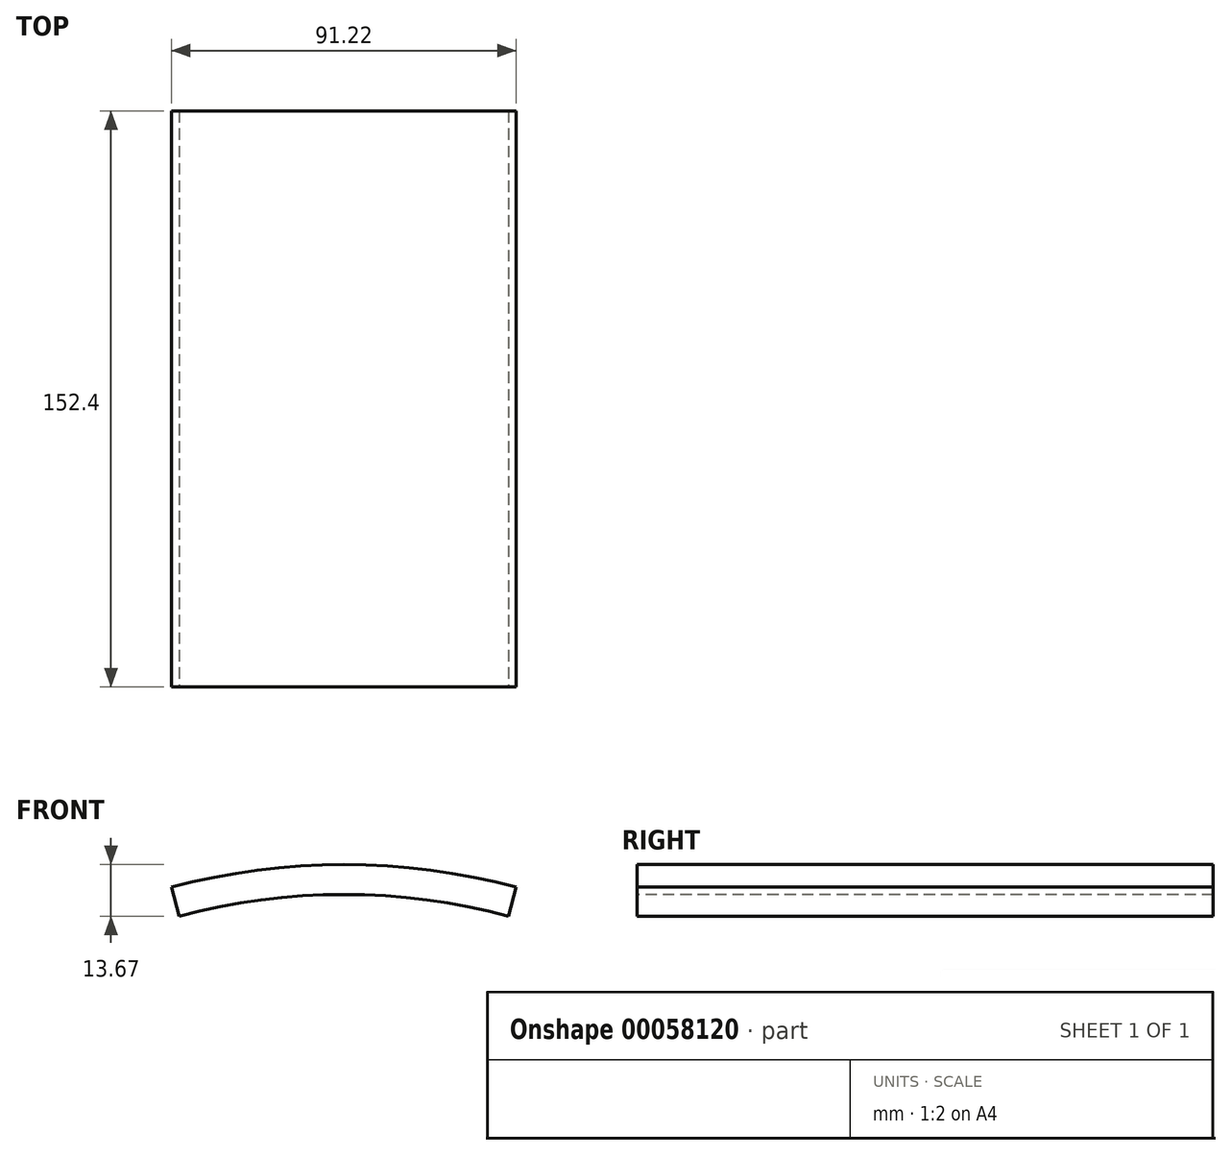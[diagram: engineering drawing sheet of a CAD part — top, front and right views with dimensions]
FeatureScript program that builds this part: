
annotation { "Feature Type Name" : "Feature", "Feature Type Description" : "" }
export const myFeature = defineFeature(function(context is Context, id is Id, definition is map)
    precondition{}
    {
        {
            var Q0;
            Q0=qCreatedBy(makeId("Front.planeOp"),FACE);
            var sketch = newSketch(context, id + "F0", { "sketchPlane" : qUnion([Q0])});
            skLineSegment(sketch, "E0.0", {"start": v(-47.64, 177.8) * mm, "end": v(47.64, 177.8) * mm});
            skPoint(sketch, "E0.0.midPoint", {"position": v(0, 177.8) * mm});
            skLineSegment(sketch, "E1.0", {"start": v(-40.84, 152.4) * mm, "end": v(40.84, 152.4) * mm});
            skPoint(sketch, "E1.0.midPoint", {"position": v(0, 152.4) * mm});
            skLineSegment(sketch, "E2", {"start": v(-47.64, 177.8) * mm, "end": v(-40.84, 152.4) * mm});
            skLineSegment(sketch, "E3", {"start": v(47.64, 177.8) * mm, "end": v(40.84, 152.4) * mm});
            skPoint(sketch, "E4.orphan", {"position": v(-130.16, 130.16) * mm});
            skPoint(sketch, "E5.orphan", {"position": v(-111.56, 111.56) * mm});
            skArc(sketch, "E6.trimOffspring", {"start": v(46.02, 171.74) * mm, "mid": v(0, 177.8) * mm, "end": v(-46.02, 171.74) * mm, "construction": true});
            skPoint(sketch, "E7.orphan", {"position": v(111.56, 111.56) * mm});
            skPoint(sketch, "E8.orphan", {"position": v(130.16, 130.16) * mm});
            skPoint(sketch, "E9.orphan", {"position": v(177.8, 47.64) * mm});
            skPoint(sketch, "E10.orphan", {"position": v(152.4, 40.84) * mm});
            skPoint(sketch, "E11.orphan", {"position": v(177.8, -47.64) * mm});
            skPoint(sketch, "E12.orphan", {"position": v(111.56, -111.56) * mm});
            skPoint(sketch, "E13.orphan", {"position": v(130.16, -130.16) * mm});
            skPoint(sketch, "E14.orphan", {"position": v(47.64, -177.8) * mm});
            skPoint(sketch, "E15.orphan", {"position": v(-40.84, -152.4) * mm});
            skPoint(sketch, "E16.orphan", {"position": v(-111.56, -111.56) * mm});
            skPoint(sketch, "E17.orphan", {"position": v(-152.4, -40.84) * mm});
            skSolve(sketch);
        }
        {
            var Q0;
            Q0 = qSketchRegion(id + "F0", true);
            extrude(context, id + "F1", {"entities" : qUnion([Q0]), "endBound" : BoundingType.SYMMETRIC, "depth" : 152.4 * mm});
        }
        {
            var Q0;
            Q0=makeQuery(id+"F1.opExtrude","CAP_FACE",FACE,{"disambiguationData":[OSD([sQuery(id+"F0.wireOp",EDGE,"E0.0"),sQuery(id+"F0.wireOp",EDGE,"E1.0"),sQuery(id+"F0.wireOp",EDGE,"E2"),sQuery(id+"F0.wireOp",EDGE,"E3")])],"isStart":false});
            var sketch = newSketch(context, id + "F2", { "sketchPlane" : qUnion([Q0])});
            skArc(sketch, "E18", {"start": v(45.6, 170.2) * mm, "mid": v(0, 176.21) * mm, "end": v(-45.6, 170.2) * mm});
            skArc(sketch, "E19", {"start": v(43.55, 162.54) * mm, "mid": v(0, 168.28) * mm, "end": v(-43.55, 162.54) * mm});
            skLineSegment(sketch, "E20.0", {"start": v(-45.6, 170.2) * mm, "end": v(-43.55, 162.54) * mm});
            skLineSegment(sketch, "E21.0", {"start": v(45.6, 170.2) * mm, "end": v(43.55, 162.54) * mm});
            skPoint(sketch, "E22.orphan", {"position": v(-47.64, 177.8) * mm});
            skPoint(sketch, "E23.orphan", {"position": v(-40.84, 152.4) * mm});
            skPoint(sketch, "E24.orphan", {"position": v(40.84, 152.4) * mm});
            skPoint(sketch, "E25.orphan", {"position": v(47.64, 177.8) * mm});
            skSolve(sketch);
        }
        {
            var Q0;
            {var subQ0=sQuery(id+"F2.wireOp",EDGE,"E18");Q0=makeQuery(id+"F2.imprint","IMPRINT",FACE,{"disambiguationData":[TD([[makeQuery(id+"F2.imprint","IMPRINT",EDGE,{"derivedFrom":subQ0}),-1.0]])]});}
            var Q1;
            {var subQ0=sQuery(id+"F2.wireOp",EDGE,"E19");Q1=makeQuery(id+"F2.imprint","IMPRINT",FACE,{"disambiguationData":[TD([[makeQuery(id+"F2.imprint","IMPRINT",EDGE,{"derivedFrom":subQ0}),1.0]])]});}
            extrude(context, id + "F3", {"entities" : qUnion([Q0, Q1]), "operationType" : NewBodyOperationType.REMOVE, "endBound" : BoundingType.UP_TO_NEXT, "oppositeDirection" : true, "depth" : 159.9 * mm});
        }
    });
